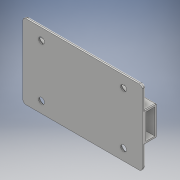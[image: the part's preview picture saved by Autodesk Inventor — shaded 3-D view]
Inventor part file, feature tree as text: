
AUTODESK INVENTOR PART (.ipt)
format: ipt  version: 2018 (Build 220112000, 112)  size: 217,088 bytes
history: native  units: mm
features: fillet x5, sketch x4, extrude x3, hole x1
ambient origin geometry x8: Origin, YZ Plane, XZ Plane, XY Plane, X Axis, Y Axis, Z Axis, Center Point
bodies: Solid1 (feature_tree)
feature tree (13):
  extrude  "Extrusion1"  Depth=50.0mm
  sketch  "Sketch2"  dims[d2=2.5mm d3=0.0mm d4=4.0mm]
  extrude  "Extrusion3"  Depth=4.0mm
  extrude  "Extrusion4"  Depth=4.0mm
  fillet  "Fillet2"  Radius=4.0mm
  fillet  "Fillet3"  Radius=55.0mm
  hole  "Hole1"  [1 undecoded]
  fillet  "Fillet4"  Radius=12.5mm
  fillet  "Fillet5"  Radius=20.0mm
  fillet  "Fillet6"  Radius=7.5mm
  sketch  "Sketch1"  dims[d0=80.0mm d1=50.0mm]
  sketch  "Sketch3"  dims[d5=4.0mm d6=4.0mm d7=4.0mm d8=55.0mm]
  sketch  "Sketch4"  dims[d9=35.0mm d10=7.5mm d11=12.5mm d14=20.0mm d15=7.5mm d16=7.5mm d17=17.0mm d18=1.5mm d19=77.5mm d20=0.0mm d21=35.0mm d22=10.0mm d23=20.0mm d24=1.5mm d25=0.0mm d27=1.0mm d28=2.0mm d29=4.0mm d30=5.984mm d31=8.0mm d32=2.0mm d33=90.0deg d34=8.0mm d35=20.594885mm d36=1.0mm d37=1.5mm d38=0.5mm]
note: 1 required parameter value undecoded (feature->parameter linkage not recoverable at this tier; creation-order binding heuristic only, values carry confidence <= 0.55)
